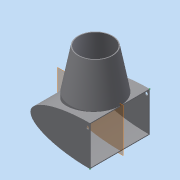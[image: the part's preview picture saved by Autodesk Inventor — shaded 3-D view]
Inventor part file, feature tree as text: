
AUTODESK INVENTOR PART (.ipt)
format: ipt  version: 2015 (Build 190159000, 159)  size: 179,200 bytes
history: native  units: in
note: dims shown in document units (in); Inventor stores cm internally (conversion verified against a paired STEP export)
features: sketch x7, extrude x4, shell x2, plane x2, revolve x1
ambient origin geometry x8: Origin, YZ Plane, XZ Plane, XY Plane, X Axis, Y Axis, Z Axis, Center Point
bodies: Solid1 (feature_tree)
feature tree (16):
  extrude  "Extrusion1"  Depth=6.0in TaperAngle=0.0deg
  shell  "Shell1"  Thickness=0.083in
  plane  "Work Plane2"
  sketch  "Sketch2"  dims[d29=2.5in d30=4.0in]
  revolve  "Revolution6"  [1 undecoded]
  extrude  "Extrusion2"  Depth=2.5in
  extrude  "Extrusion3"  Depth=2.5in
  shell  "Shell6"  Thickness=4.0in
  plane  "Work Plane6"
  sketch  "Sketch5"  dims[d49=1.75in d50=90.0deg]
  sketch  "Sketch6"  dims[d51=6.0in d52=0.0in]
  extrude  "Extrusion4"  TaperAngle=90.0deg  [1 undecoded]
  sketch  "Sketch1"  dims[d0=4.0in d2=6.0in d3=0.0in d4=0.083in]
  sketch  "Sketch3"  dims[d31=1.75in d35=2.5in]
  sketch  "Sketch4"  dims[d38=0.6914in d47=2.5in d48=4.0in]
  sketch  "Sketch7"  dims[d53=5.0in d54=6.0in d55=0.0in d56=0.083in d57=0.3125in d58=0.25in d59=3.5in d60=1.0in d61=0.0in]
note: 2 required parameter values undecoded (feature->parameter linkage not recoverable at this tier; creation-order binding heuristic only, values carry confidence <= 0.55)